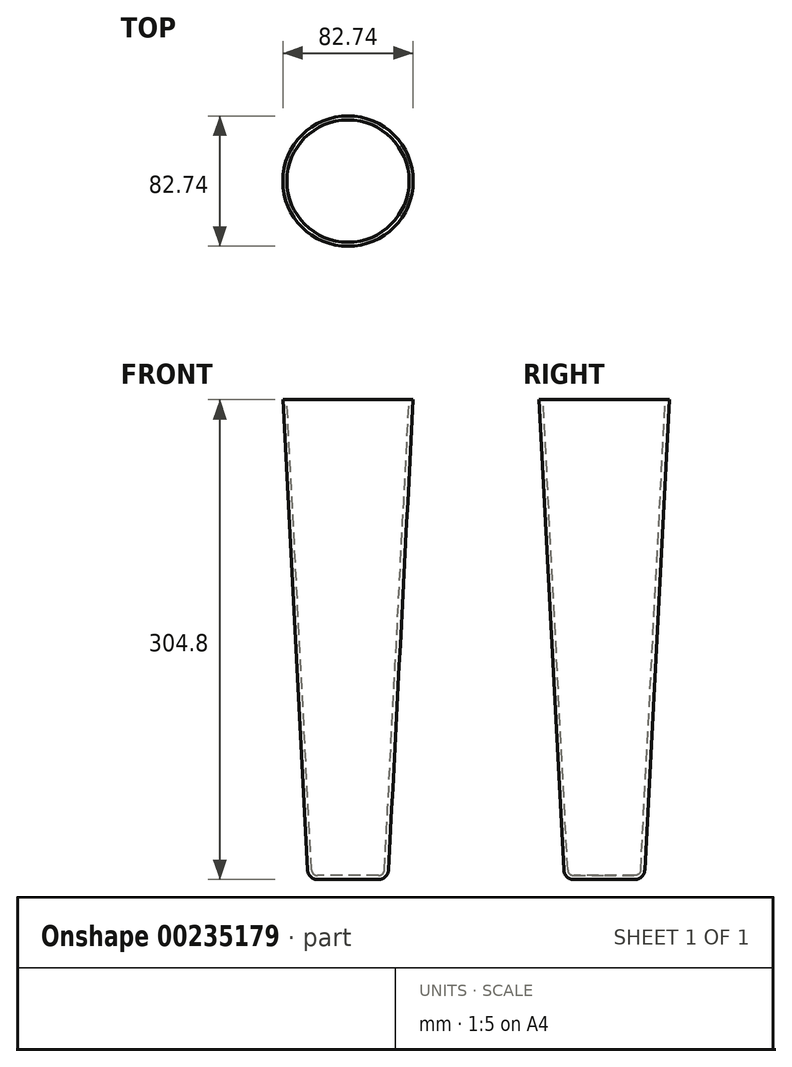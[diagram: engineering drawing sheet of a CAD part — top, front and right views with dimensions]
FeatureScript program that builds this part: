
annotation { "Feature Type Name" : "Feature", "Feature Type Description" : "" }
export const myFeature = defineFeature(function(context is Context, id is Id, definition is map)
    precondition{}
    {
        {
            var Q0;
            Q0=qCreatedBy(makeId("Top.planeOp"),FACE);
            var sketch = newSketch(context, id + "F0", { "sketchPlane" : qUnion([Q0])});
            skCircle(sketch, "E0", {"center": v(0, 0) * mm, "radius": 25.4 * mm});
            skSolve(sketch);
        }
        {
            var Q0;
            Q0 = qSketchRegion(id + "F0", true);
            extrude(context, id + "F1", {"entities" : qUnion([Q0]), "depth" : 304.8 * mm, "hasDraft" : true, "draftAngle" : 3 * degree});
        }
        {
            var Q0;
            Q0=makeQuery(id+"F1.opExtrude","CAP_FACE",FACE,{"disambiguationData":[OSD([sQuery(id+"F0.wireOp",EDGE,"E0")])],"isStart":true});
            fillet(context, id + "F2", {"entities" : qUnion([Q0]), "radius" : 6.35 * mm, "tangentPropagation" : true, "allowEdgeOverflow" : false});
        }
        {
            var Q0;
            Q0=makeQuery(id+"F1.opExtrude","CAP_FACE",FACE,{"disambiguationData":[OSD([sQuery(id+"F0.wireOp",EDGE,"E0")])],"isStart":false});
            shell(context, id + "F3", {"entities" : qUnion([Q0]), "thickness" : 2.54 * mm});
        }
    });
